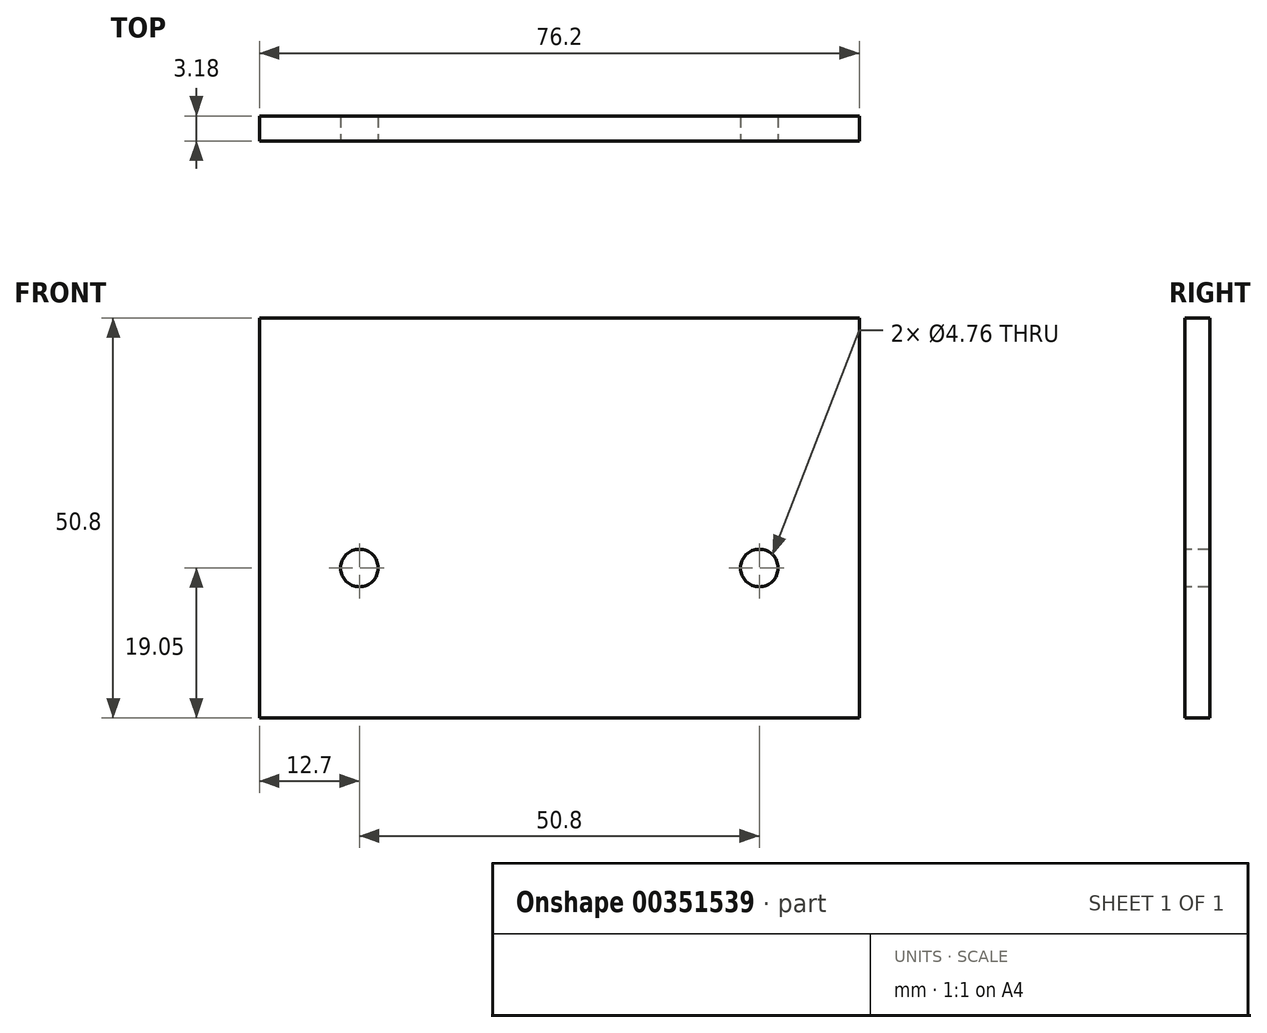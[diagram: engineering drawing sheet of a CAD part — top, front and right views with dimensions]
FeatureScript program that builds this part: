
annotation { "Feature Type Name" : "Feature", "Feature Type Description" : "" }
export const myFeature = defineFeature(function(context is Context, id is Id, definition is map)
    precondition{}
    {
        {
            var Q0;
            Q0=qCreatedBy(makeId("Front.planeOp"),FACE);
            var sketch = newSketch(context, id + "F0", { "sketchPlane" : qUnion([Q0])});
            skLineSegment(sketch, "E0.bottom", {"start": v(38.1, 25.4) * mm, "end": v(-38.1, 25.4) * mm});
            skLineSegment(sketch, "E0.top", {"start": v(38.1, -25.4) * mm, "end": v(-38.1, -25.4) * mm});
            skLineSegment(sketch, "E0.left", {"start": v(38.1, 25.4) * mm, "end": v(38.1, -25.4) * mm});
            skLineSegment(sketch, "E0.right", {"start": v(-38.1, 25.4) * mm, "end": v(-38.1, -25.4) * mm});
            skPoint(sketch, "E0.middle", {"position": v(0, 0) * mm});
            skSolve(sketch);
        }
        {
            var Q0;
            Q0 = qSketchRegion(id + "F0", true);
            extrude(context, id + "F1", {"entities" : qUnion([Q0]), "depth" : 3.17 * mm, "symmetric" : true});
        }
        {
            var Q0;
            Q0=makeQuery(id+"F1.opExtrude","CAP_FACE",FACE,{"disambiguationData":[OSD([sQuery(id+"F0.wireOp",EDGE,"E0.bottom"),sQuery(id+"F0.wireOp",EDGE,"E0.top"),sQuery(id+"F0.wireOp",EDGE,"E0.left"),sQuery(id+"F0.wireOp",EDGE,"E0.right")])],"isStart":false});
            var sketch = newSketch(context, id + "F2", { "sketchPlane" : qUnion([Q0])});
            skCircle(sketch, "E1", {"center": v(25.4, -6.35) * mm, "radius": 2.38 * mm});
            skCircle(sketch, "E2", {"center": v(-25.4, -6.35) * mm, "radius": 2.38 * mm});
            skSolve(sketch);
        }
        {
            var Q0;
            Q0 = qSketchRegion(id + "F2", true);
            extrude(context, id + "F3", {"entities" : qUnion([Q0]), "operationType" : NewBodyOperationType.REMOVE, "endBound" : BoundingType.THROUGH_ALL, "oppositeDirection" : true, "depth" : 25.4 * mm});
        }
    });
